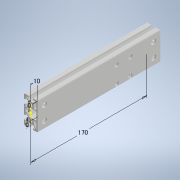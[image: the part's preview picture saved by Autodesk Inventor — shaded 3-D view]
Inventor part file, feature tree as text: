
AUTODESK INVENTOR PART (.ipt)
format: ipt  version: 2022 (Build 260153000, 153)  size: 514,048 bytes
history: native  units: mm
features: sketch x9, hole x8, other x7, extrude x1, pattern_linear x1
ambient origin geometry x8: Origin, YZ Plane, XZ Plane, XY Plane, X Axis, Y Axis, Z Axis, Center Point
bodies: Solid1 (feature_tree)
feature tree (26):
  extrude  "Extrusion1"  Depth=10.0mm TaperAngle=0.0deg
  hole  "Hole1"  [1 undecoded]
  pattern_linear  "Rectangular Pattern1"  Spacing1=3.0mm  [1 undecoded]
  hole  "Hole2"  [1 undecoded]
  hole  "Hole3"  [1 undecoded]
  hole  "Hole6"  [1 undecoded]
  hole  "Hole7"  [1 undecoded]
  other  "C1_XY"
  other  "C1_YZ"
  other  "C1_ZX"
  other  "C1_X"
  other  "C1_Y"
  other  "C1_Z"
  other  "C1_Center"
  sketch  "スケッチ10"
  hole  "穴10"  [1 undecoded]
  hole  "穴12"  [1 undecoded]
  hole  "穴13"  [1 undecoded]
  sketch  "Sketch_63"  dims[d50=7.35mm d51=6.0mm d52=4.0mm d53=2.0mm d54=90.0deg d55=20.0mm d56=0.0mm d64=0.0mm d65=3.0mm d66=136.0mm d67=20.0mm d69=20.0mm d70=20.0mm d72=24.0mm d86=3.5mm d87=6.0mm d88=6.0mm d89=2.0mm d90=90.0deg d91=4.0mm d92=20.594885mm d100=10.0mm d101=3.0mm d102=20.0mm d103=10.0mm d104=170.0mm d105=9.0mm d106=6.0mm d107=4.0mm d108=2.0mm d109=90.0deg d110=5.5mm d111=20.594885mm d112=6.0mm d113=6.0mm d114=4.0mm d115=2.0mm d116=90.0deg d117=5.5mm d118=20.594885mm]
  sketch  "Sketch2"  dims[d0=180.0mm d1=0.0mm]
  sketch  "Sketch3"  dims[d2=4.2mm d3=6.0mm d4=4.0mm d5=2.0mm d6=90.0deg d7=180.0mm d8=0.0mm d9=20.0mm d11=20.0mm d12=10.0mm d14=0.0mm]
  sketch  "Sketch4"  dims[d15=7.35mm d16=6.0mm d17=4.0mm d18=2.0mm d19=90.0deg d20=20.0mm d21=0.0mm]
  sketch  "Sketch7"  dims[d22=7.35mm d23=6.0mm d24=4.0mm d25=2.0mm d26=90.0deg d27=20.0mm d28=0.0mm]
  sketch  "Sketch8"  dims[d43=7.35mm d44=6.0mm d45=4.0mm d46=2.0mm d47=90.0deg d48=20.0mm d49=0.0mm]
  sketch  "スケッチ12"
  sketch  "スケッチ13"
note: 9 required parameter values undecoded (feature->parameter linkage not recoverable at this tier; creation-order binding heuristic only, values carry confidence <= 0.55)
